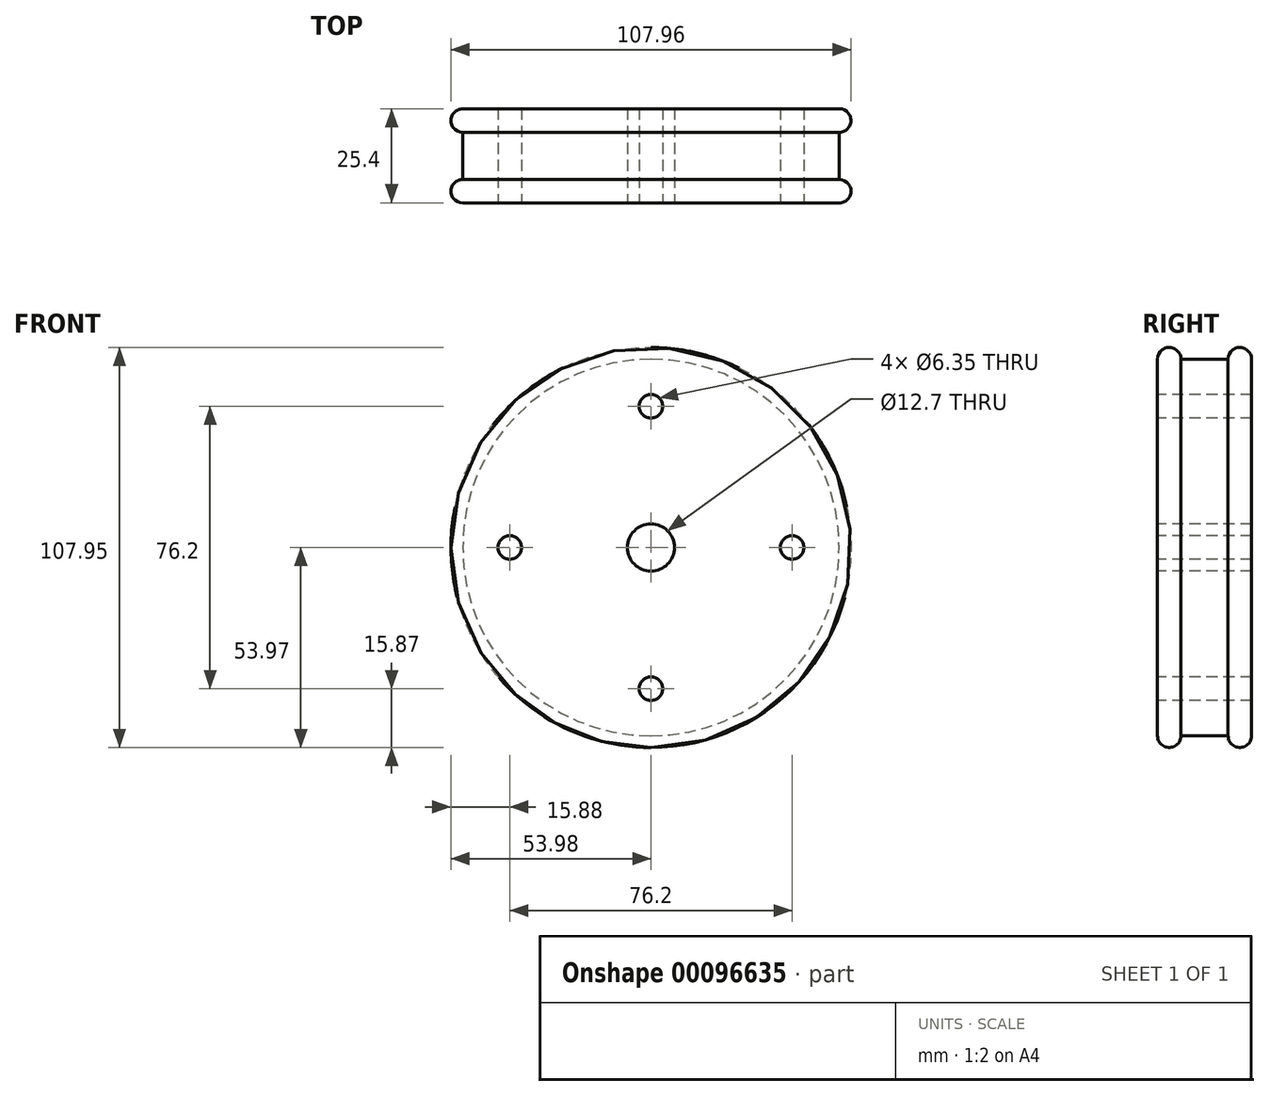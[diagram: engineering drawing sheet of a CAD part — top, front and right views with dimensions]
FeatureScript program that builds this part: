
annotation { "Feature Type Name" : "Feature", "Feature Type Description" : "" }
export const myFeature = defineFeature(function(context is Context, id is Id, definition is map)
    precondition{}
    {
        {
            var Q0;
            Q0=qCreatedBy(makeId("Front.planeOp"),FACE);
            var sketch = newSketch(context, id + "F0", { "sketchPlane" : qUnion([Q0])});
            skCircle(sketch, "E0", {"center": v(0, 0) * mm, "radius": 50.8 * mm});
            skSolve(sketch);
        }
        {
            var Q0;
            Q0=makeQuery(id+"F0.imprint","IMPRINT",FACE,{"disambiguationData":[TD([[makeQuery(id+"F0.imprint","IMPRINT",EDGE,{"derivedFrom":sQuery(id+"F0.wireOp",EDGE,"E0")}),1.0]])]});
            extrude(context, id + "F1", {"entities" : qUnion([Q0]), "depth" : 25.4 * mm});
        }
        {
            var Q0;
            Q0=makeQuery(id+"F1.opExtrude","CAP_FACE",FACE,{"disambiguationData":[OSD([sQuery(id+"F0.wireOp",EDGE,"E0")])],"isStart":false});
            var sketch = newSketch(context, id + "F2", { "sketchPlane" : qUnion([Q0])});
            skCircle(sketch, "E1", {"center": v(0, 0) * mm, "radius": 53.98 * mm});
            skSolve(sketch);
        }
        {
            var Q0;
            Q0 = qSketchRegion(id + "F2", true);
            extrude(context, id + "F3", {"entities" : qUnion([Q0]), "operationType" : NewBodyOperationType.ADD, "oppositeDirection" : true, "depth" : 6.35 * mm});
        }
        {
            var Q0;
            Q0=makeQuery(id+"F1.opExtrude","CAP_FACE",FACE,{"disambiguationData":[OSD([sQuery(id+"F0.wireOp",EDGE,"E0")])],"isStart":true});
            var sketch = newSketch(context, id + "F4", { "sketchPlane" : qUnion([Q0])});
            skCircle(sketch, "E2.0", {"center": v(0, 0) * mm, "radius": 53.98 * mm});
            skSolve(sketch);
        }
        {
            var Q0;
            Q0 = qSketchRegion(id + "F4", true);
            extrude(context, id + "F5", {"entities" : qUnion([Q0]), "operationType" : NewBodyOperationType.ADD, "oppositeDirection" : true, "depth" : 6.35 * mm});
        }
        {
            var Q0;
            Q0=makeQuery(id+"F5.opExtrude","CAP_EDGE",EDGE,{"disambiguationData":[OSD([sQuery(id+"F4.wireOp",EDGE,"E2.0")])],"isStart":true});
            var Q1;
            Q1=makeQuery(id+"F5.opExtrude","CAP_EDGE",EDGE,{"disambiguationData":[OSD([sQuery(id+"F4.wireOp",EDGE,"E2.0")])],"isStart":false});
            var Q2;
            Q2=makeQuery(id+"F3.opExtrude","CAP_EDGE",EDGE,{"disambiguationData":[OSD([sQuery(id+"F2.wireOp",EDGE,"E1")])],"isStart":true});
            var Q3;
            Q3=makeQuery(id+"F3.opExtrude","CAP_EDGE",EDGE,{"disambiguationData":[OSD([sQuery(id+"F2.wireOp",EDGE,"E1")])],"isStart":false});
            fillet(context, id + "F6", {"entities" : qUnion([Q0, Q1, Q2, Q3]), "radius" : 3.17 * mm, "tangentPropagation" : true, "allowEdgeOverflow" : false});
        }
        {
            var Q0;
            Q0=makeQuery(id+"F3.boolean.opBoolean","MERGE",FACE,{"derivedFrom":[makeQuery(id+"F1.opExtrude","CAP_FACE",FACE,{"disambiguationData":[OSD([sQuery(id+"F0.wireOp",EDGE,"E0")])],"isStart":false}),makeQuery(id+"F3.opExtrude","CAP_FACE",FACE,{"disambiguationData":[OSD([sQuery(id+"F2.wireOp",EDGE,"E1")])],"isStart":true})]});
            var sketch = newSketch(context, id + "F7", { "sketchPlane" : qUnion([Q0])});
            skCircle(sketch, "E3", {"center": v(0, 0) * mm, "radius": 6.35 * mm});
            skSolve(sketch);
        }
        {
            var Q0;
            Q0=makeQuery(id+"F7.imprint","IMPRINT",FACE,{"disambiguationData":[TD([[makeQuery(id+"F7.imprint","IMPRINT",EDGE,{"derivedFrom":sQuery(id+"F7.wireOp",EDGE,"E3")}),1.0]])]});
            extrude(context, id + "F8", {"entities" : qUnion([Q0]), "operationType" : NewBodyOperationType.REMOVE, "oppositeDirection" : true, "depth" : 25.4 * mm});
        }
        {
            var Q0;
            Q0=makeQuery(id+"F3.boolean.opBoolean","MERGE",FACE,{"derivedFrom":[makeQuery(id+"F1.opExtrude","CAP_FACE",FACE,{"disambiguationData":[OSD([sQuery(id+"F0.wireOp",EDGE,"E0")])],"isStart":false}),makeQuery(id+"F3.opExtrude","CAP_FACE",FACE,{"disambiguationData":[OSD([sQuery(id+"F2.wireOp",EDGE,"E1")])],"isStart":true})]});
            var sketch = newSketch(context, id + "F9", { "sketchPlane" : qUnion([Q0])});
            skPoint(sketch, "E4", {"position": v(0, 38.1) * mm});
            skPoint(sketch, "E5", {"position": v(38.1, 0) * mm});
            skPoint(sketch, "E6", {"position": v(-38.1, 0) * mm});
            skPoint(sketch, "E7", {"position": v(0, -38.1) * mm});
            skSolve(sketch);
        }
        {
            var Q0;
            Q0=sQuery(id+"F9.wireOp",VERTEX,"E4");
            var Q1;
            Q1=sQuery(id+"F9.wireOp",VERTEX,"E5");
            var Q2;
            Q2=sQuery(id+"F9.wireOp",VERTEX,"E7");
            var Q3;
            Q3=sQuery(id+"F9.wireOp",VERTEX,"E6");
            var Q4;
            Q4=makeQuery(id+"F1.opExtrude","SWEPT_BODY",BODY,{"disambiguationData":[OSD([sQuery(id+"F0.wireOp",EDGE,"E0")])]});
            hole(context, id + "F10", {"style" : HoleStyle.SIMPLE, "endStyle" : HoleEndStyle.THROUGH, "holeDiameter" : 6.35 * mm, "locations" : qUnion([Q0, Q1, Q2, Q3]), "scope" : qUnion([Q4]), "isTappedThrough" : true});
        }
    });
